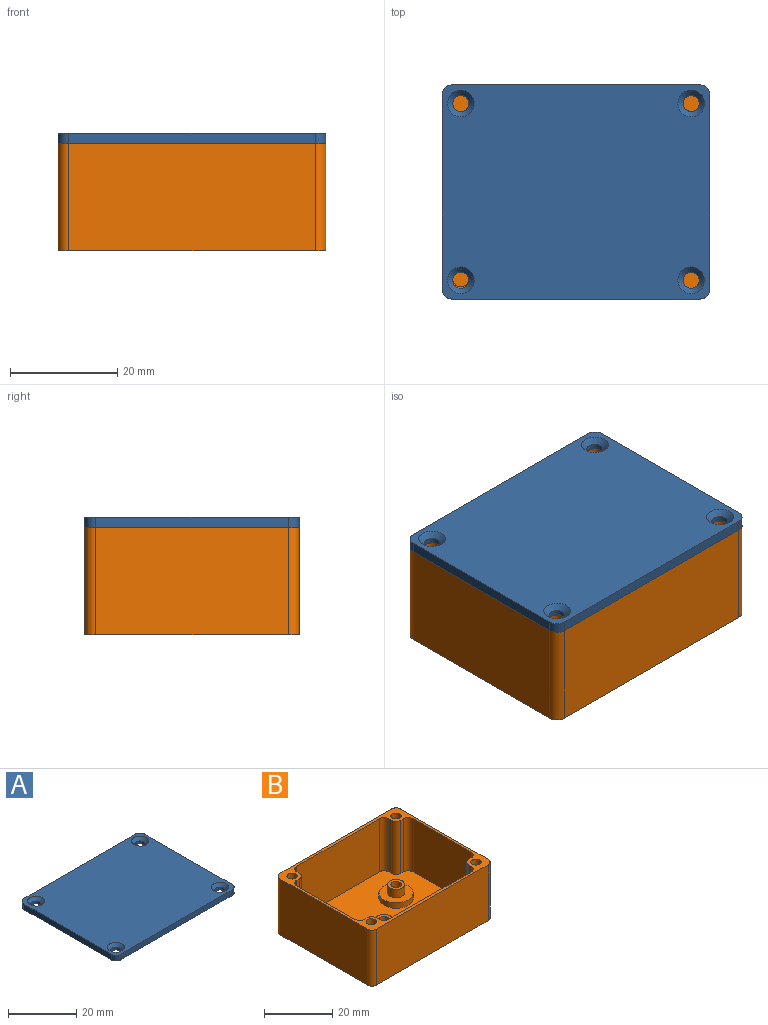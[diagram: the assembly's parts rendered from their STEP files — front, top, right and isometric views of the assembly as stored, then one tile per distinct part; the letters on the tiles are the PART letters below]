
ASSEMBLY  parts=2 mates=1
PART A: 18 faces, bbox 50x40x2 mm
  f0: plane 36x2mm, normal (-1,0,0), area 72mm2, adj f4,f5,f14,f17
  f1: plane 46x2mm, normal (0,-1,0), area 92mm2, adj f4,f5,f14,f15
  f2: plane 36x2mm, normal (1,0,0), area 72mm2, adj f4,f5,f15,f16
  f3: plane 46x2mm, normal (0,1,0), area 92mm2, adj f4,f5,f16,f17
  f4: plane 50x40mm, normal (0,0,1), area 1918mm2, adj f0,f1,f2,f3,f10,f11,f12,f13
  f5: plane 50x40mm, normal (0,0,-1), area 1968.3mm2, adj f0,f1,f2,f3,f6,f7,f8,f9
  f6: cylinder r=1.5mm len=3mm, axis (0,0,1), area 9.4mm2, adj f5,f13
  f7: cylinder r=1.5mm len=3mm, axis (0,0,1), area 9.4mm2, adj f5,f12
  f8: cylinder r=1.5mm len=3mm, axis (0,0,1), area 9.4mm2, adj f5,f11
  f9: cylinder r=1.5mm len=3mm, axis (0,0,1), area 9.4mm2, adj f5,f10
  f10: cone r=1.5mm half-angle=45deg, axis (0,0,1), area 17.8mm2, adj f4,f9
  f11: cone r=1.5mm half-angle=45deg, axis (0,0,1), area 17.8mm2, adj f4,f8
  f12: cone r=1.5mm half-angle=45deg, axis (0,0,1), area 17.8mm2, adj f4,f7
  f13: cone r=1.5mm half-angle=45deg, axis (0,0,1), area 17.8mm2, adj f4,f6
  f14: cylinder r=2mm len=2mm, axis (0,0,1), area 6.3mm2, adj f0,f1,f4,f5
  f15: cylinder r=2mm len=2mm, axis (0,0,-1), area 6.3mm2, adj f1,f2,f4,f5
  f16: cylinder r=2mm len=2mm, axis (0,0,1), area 6.3mm2, adj f2,f3,f4,f5
  f17: cylinder r=2mm len=2mm, axis (0,0,-1), area 6.3mm2, adj f0,f3,f4,f5
PART B: 67 faces, bbox 50x40x20 mm
  f0: plane 50x40mm, normal (0,0,-1), area 1949.8mm2, adj f6,f7,f8,f9,f37,f38,f39,f40
  f1: plane 48x38mm, normal (0,0,1), area 1563.5mm2, adj f2,f3,f4,f5,f11,f12,f13,f14
  f2: plane 34x19mm, normal (0,-1,0), area 646mm2, adj f1,f10,f57,f64
  f3: plane 24x19mm, normal (-1,0,0), area 456mm2, adj f1,f10,f55,f59
  f4: plane 34x19mm, normal (0,1,0), area 646mm2, adj f1,f10,f60,f61
  f5: plane 24x19mm, normal (1,0,0), area 456mm2, adj f1,f10,f63,f65
  f6: plane 36x20mm, normal (-1,0,0), area 720mm2, adj f0,f10,f51,f54
  f7: plane 46x20mm, normal (0,-1,0), area 920mm2, adj f0,f10,f51,f52
  f8: plane 36x20mm, normal (1,0,0), area 720mm2, adj f0,f10,f52,f53
  f9: plane 46x20mm, normal (0,1,0), area 920mm2, adj f0,f10,f53,f54
  f10: plane 50x40mm, normal (0,0,1), area 247.7mm2, adj f2,f3,f4,f5,f6,f7,f8,f9
  f11: plane 19x1mm, normal (1,0,0), area 19mm2, adj f1,f10,f64,f66
  f12: plane 19x1mm, normal (0,-1,0), area 19mm2, adj f1,f10,f65,f66
  f13: plane 19x1mm, normal (1,0,0), area 19mm2, adj f1,f10,f61,f62
  f14: plane 19x1mm, normal (0,1,0), area 19mm2, adj f1,f10,f62,f63
  f15: plane 19x1mm, normal (-1,0,0), area 19mm2, adj f1,f10,f58,f60
  f16: plane 19x1mm, normal (0,1,0), area 19mm2, adj f1,f10,f58,f59
  f17: plane 19x1mm, normal (-1,0,0), area 19mm2, adj f1,f10,f56,f57
  f18: plane 19x1mm, normal (0,-1,0), area 19mm2, adj f1,f10,f55,f56
  f19: cylinder r=1.5mm len=10mm, axis (0,0,1), area 94.2mm2, adj f10,f20
  f20: plane 3x3mm, normal (0,0,1), area 7.1mm2, adj f19
  f21: cylinder r=1.5mm len=10mm, axis (0,0,1), area 94.2mm2, adj f10,f22
  f22: plane 3x3mm, normal (0,0,1), area 7.1mm2, adj f21
  f23: cylinder r=1.5mm len=10mm, axis (0,0,1), area 94.2mm2, adj f10,f24
  f24: plane 3x3mm, normal (0,0,1), area 7.1mm2, adj f23
  f25: cylinder r=1.5mm len=10mm, axis (0,0,1), area 94.2mm2, adj f10,f26
  f26: plane 3x3mm, normal (0,0,1), area 7.1mm2, adj f25
  f27: cylinder r=1.5mm len=4mm, axis (0,0,-1), area 37.7mm2, adj f29,f50
  f28: cylinder r=2.5mm len=5mm, axis (0,0,-1), area 47.1mm2, adj f29,f34
  f29: plane 5x5mm, normal (0,0,1), area 12.6mm2, adj f27,f28
  f30: cylinder r=1.5mm len=4mm, axis (0,0,-1), area 37.7mm2, adj f32,f43
  f31: cylinder r=2.5mm len=5mm, axis (0,0,-1), area 47.1mm2, adj f32,f36
  f32: plane 5x5mm, normal (0,0,1), area 12.6mm2, adj f30,f31
  f33: cylinder r=5mm len=10mm, axis (0,0,-1), area 62.8mm2, adj f1,f34
  f34: plane 10x10mm, normal (0,0,1), area 58.9mm2, adj f28,f33
  f35: cylinder r=5mm len=10mm, axis (0,0,-1), area 62.8mm2, adj f1,f36
  f36: plane 10x10mm, normal (0,0,1), area 58.9mm2, adj f31,f35
  f37: plane 2.6x2mm, normal (0.5,0.87,0), area 6mm2, adj f0,f38,f42,f43
  f38: plane 3x2mm, normal (1,0,0), area 6mm2, adj f0,f37,f39,f43
  f39: plane 2.6x2mm, normal (0.5,-0.87,0), area 6mm2, adj f0,f38,f40,f43
  f40: plane 2.6x2mm, normal (-0.5,-0.87,0), area 6mm2, adj f0,f39,f41,f43
  f41: plane 3x2mm, normal (-1,0,0), area 6mm2, adj f0,f40,f42,f43
  f42: plane 2.6x2mm, normal (-0.5,0.87,0), area 6mm2, adj f0,f37,f41,f43
  f43: plane 6x5.2mm, normal (0,0,-1), area 16.3mm2, adj f30,f37,f38,f39,f40,f41,f42
  f44: plane 2.6x2mm, normal (0.5,0.87,0), area 6mm2, adj f0,f45,f49,f50
  f45: plane 3x2mm, normal (1,0,0), area 6mm2, adj f0,f44,f46,f50
  f46: plane 2.6x2mm, normal (0.5,-0.87,0), area 6mm2, adj f0,f45,f47,f50
  f47: plane 2.6x2mm, normal (-0.5,-0.87,0), area 6mm2, adj f0,f46,f48,f50
  f48: plane 3x2mm, normal (-1,0,0), area 6mm2, adj f0,f47,f49,f50
  f49: plane 2.6x2mm, normal (-0.5,0.87,0), area 6mm2, adj f0,f44,f48,f50
  f50: plane 6x5.2mm, normal (0,0,-1), area 16.3mm2, adj f27,f44,f45,f46,f47,f48,f49
  f51: cylinder r=2mm len=20mm, axis (0,0,1), area 62.8mm2, adj f0,f6,f7,f10
  f52: cylinder r=2mm len=20mm, axis (0,0,-1), area 62.8mm2, adj f0,f7,f8,f10
  f53: cylinder r=2mm len=20mm, axis (0,0,1), area 62.8mm2, adj f0,f8,f9,f10
  f54: cylinder r=2mm len=20mm, axis (0,0,-1), area 62.8mm2, adj f0,f6,f9,f10
  f55: cylinder r=2mm len=19mm, axis (0,0,-1), area 59.7mm2, adj f1,f3,f10,f18
  f56: cylinder r=2mm len=19mm, axis (0,0,1), area 59.7mm2, adj f1,f10,f17,f18
  f57: cylinder r=2mm len=19mm, axis (0,0,1), area 59.7mm2, adj f1,f2,f10,f17
  f58: cylinder r=2mm len=19mm, axis (0,0,1), area 59.7mm2, adj f1,f10,f15,f16
  f59: cylinder r=2mm len=19mm, axis (0,0,1), area 59.7mm2, adj f1,f3,f10,f16
  f60: cylinder r=2mm len=19mm, axis (0,0,1), area 59.7mm2, adj f1,f4,f10,f15
  f61: cylinder r=2mm len=19mm, axis (0,0,-1), area 59.7mm2, adj f1,f4,f10,f13
  f62: cylinder r=2mm len=19mm, axis (0,0,1), area 59.7mm2, adj f1,f10,f13,f14
  f63: cylinder r=2mm len=19mm, axis (0,0,1), area 59.7mm2, adj f1,f5,f10,f14
  f64: cylinder r=2mm len=19mm, axis (0,0,-1), area 59.7mm2, adj f1,f2,f10,f11
  f65: cylinder r=2mm len=19mm, axis (0,0,-1), area 59.7mm2, adj f1,f5,f10,f12
  f66: cylinder r=2mm len=19mm, axis (0,0,1), area 59.7mm2, adj f1,f10,f11,f12
PLACE A t=(-68.99,-19.07,17.4)mm
PLACE B t=(28.8,-15.27,-2.6)mm
MATE slider B.f23 <-> A.f8  axis (0,0,1) through (1.87,-15.57,17.4)mm
